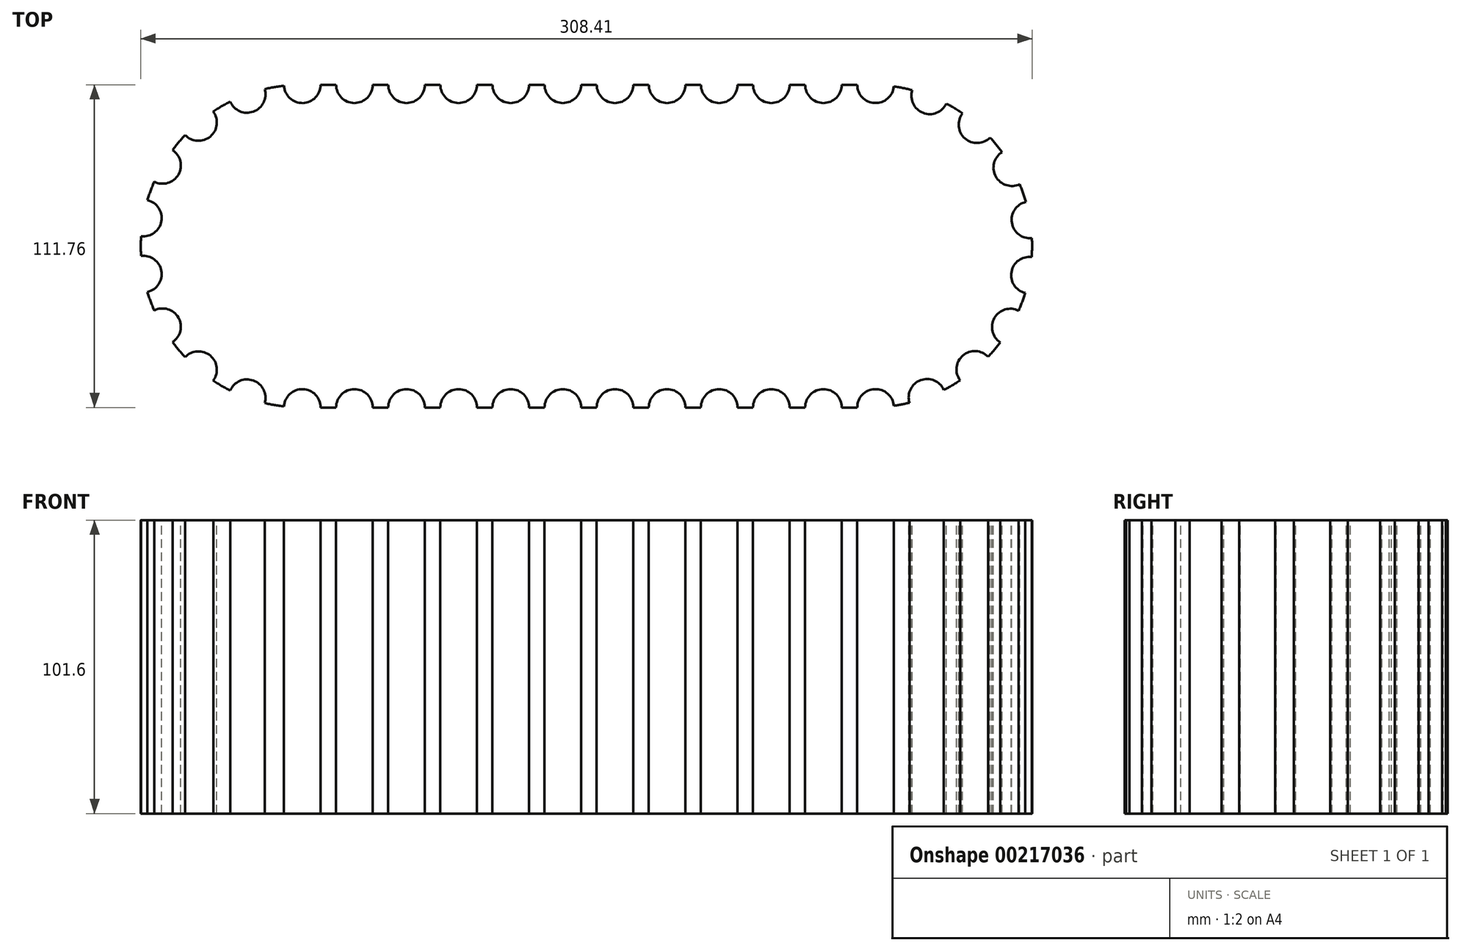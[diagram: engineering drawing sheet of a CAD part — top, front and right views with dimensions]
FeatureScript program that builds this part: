
annotation { "Feature Type Name" : "Feature", "Feature Type Description" : "" }
export const myFeature = defineFeature(function(context is Context, id is Id, definition is map)
    precondition{}
    {
        {
            var Q0;
            Q0=qCreatedBy(makeId("Top.planeOp"),FACE);
            var sketch = newSketch(context, id + "F0", { "sketchPlane" : qUnion([Q0])});
            skArc(sketch, "E0", {"start": v(-196.65, 55.88) * mm, "mid": v(-252.53, 0) * mm, "end": v(-196.65, -55.88) * mm});
            skArc(sketch, "E1", {"start": v(0, -55.88) * mm, "mid": v(55.88, 0) * mm, "end": v(0, 55.88) * mm});
            skLineSegment(sketch, "E2", {"start": v(-196.65, 55.88) * mm, "end": v(0, 55.88) * mm});
            skLineSegment(sketch, "E3", {"start": v(-196.65, -55.88) * mm, "end": v(0, -55.88) * mm});
            skSolve(sketch);
        }
        {
            var Q0;
            Q0=makeQuery(id+"F0.imprint","IMPRINT",FACE,{"disambiguationData":[TD([[makeQuery(id+"F0.imprint","IMPRINT",EDGE,{"derivedFrom":sQuery(id+"F0.wireOp",EDGE,"E0")}),1.0]])]});
            extrude(context, id + "F1", {"entities" : qUnion([Q0]), "depth" : 101.6 * mm});
        }
        {
            var Q0;
            Q0=makeQuery(id+"F1.opExtrude","CAP_FACE",FACE,{"disambiguationData":[OSD([sQuery(id+"F0.wireOp",EDGE,"E0"),sQuery(id+"F0.wireOp",EDGE,"E1"),sQuery(id+"F0.wireOp",EDGE,"E2"),sQuery(id+"F0.wireOp",EDGE,"E3")])],"isStart":false});
            var sketch = newSketch(context, id + "F2", { "sketchPlane" : qUnion([Q0])});
            skCircle(sketch, "E4", {"center": v(-196.65, 55.88) * mm, "radius": 6.35 * mm});
            skCircle(sketch, "E5.1.0.0", {"center": v(-178.61, 55.88) * mm, "radius": 6.35 * mm});
            skCircle(sketch, "E5.2.0.0", {"center": v(-160.58, 55.88) * mm, "radius": 6.35 * mm});
            skCircle(sketch, "E5.3.0.0", {"center": v(-142.54, 55.88) * mm, "radius": 6.35 * mm});
            skCircle(sketch, "E5.4.0.0", {"center": v(-124.51, 55.88) * mm, "radius": 6.35 * mm});
            skCircle(sketch, "E5.5.0.0", {"center": v(-106.48, 55.88) * mm, "radius": 6.35 * mm});
            skCircle(sketch, "E5.6.0.0", {"center": v(-88.44, 55.88) * mm, "radius": 6.35 * mm});
            skCircle(sketch, "E5.7.0.0", {"center": v(-70.4, 55.88) * mm, "radius": 6.35 * mm});
            skCircle(sketch, "E5.8.0.0", {"center": v(-52.37, 55.88) * mm, "radius": 6.35 * mm});
            skCircle(sketch, "E5.9.0.0", {"center": v(-34.34, 55.88) * mm, "radius": 6.35 * mm});
            skCircle(sketch, "E5.10.0.0", {"center": v(-16.3, 55.88) * mm, "radius": 6.35 * mm});
            skCircle(sketch, "E5.11.0.0", {"center": v(1.73, 55.88) * mm, "radius": 6.35 * mm});
            skLineSegment(sketch, "E5.direction1", {"start": v(-196.65, 55.88) * mm, "end": v(-178.61, 55.88) * mm, "construction": true});
            skCircle(sketch, "E6", {"center": v(-196.65, -55.88) * mm, "radius": 6.35 * mm});
            skCircle(sketch, "E7.1.0.0", {"center": v(-178.61, -55.88) * mm, "radius": 6.35 * mm});
            skCircle(sketch, "E7.2.0.0", {"center": v(-160.58, -55.88) * mm, "radius": 6.35 * mm});
            skCircle(sketch, "E7.3.0.0", {"center": v(-142.54, -55.88) * mm, "radius": 6.35 * mm});
            skCircle(sketch, "E7.4.0.0", {"center": v(-124.51, -55.88) * mm, "radius": 6.35 * mm});
            skCircle(sketch, "E7.5.0.0", {"center": v(-106.48, -55.88) * mm, "radius": 6.35 * mm});
            skCircle(sketch, "E7.6.0.0", {"center": v(-88.44, -55.88) * mm, "radius": 6.35 * mm});
            skCircle(sketch, "E7.7.0.0", {"center": v(-70.4, -55.88) * mm, "radius": 6.35 * mm});
            skCircle(sketch, "E7.8.0.0", {"center": v(-52.37, -55.88) * mm, "radius": 6.35 * mm});
            skCircle(sketch, "E7.9.0.0", {"center": v(-34.34, -55.88) * mm, "radius": 6.35 * mm});
            skCircle(sketch, "E7.10.0.0", {"center": v(-16.3, -55.88) * mm, "radius": 6.35 * mm});
            skCircle(sketch, "E7.11.0.0", {"center": v(1.73, -55.88) * mm, "radius": 6.35 * mm});
            skLineSegment(sketch, "E7.direction1", {"start": v(-196.65, -55.88) * mm, "end": v(-178.61, -55.88) * mm, "construction": true});
            skCircle(sketch, "E8.1.0", {"center": v(-215.76, 52.51) * mm, "radius": 6.35 * mm});
            skCircle(sketch, "E8.2.0", {"center": v(-232.57, 42.8) * mm, "radius": 6.35 * mm});
            skCircle(sketch, "E8.3.0", {"center": v(-245.04, 27.94) * mm, "radius": 6.35 * mm});
            skCircle(sketch, "E8.4.0", {"center": v(-251.68, 9.7) * mm, "radius": 6.35 * mm});
            skCircle(sketch, "E8.5.0", {"center": v(-251.68, -9.7) * mm, "radius": 6.35 * mm});
            skCircle(sketch, "E8.6.0", {"center": v(-245.04, -27.94) * mm, "radius": 6.35 * mm});
            skCircle(sketch, "E8.7.0", {"center": v(-232.57, -42.8) * mm, "radius": 6.35 * mm});
            skCircle(sketch, "E8.8.0", {"center": v(-215.76, -52.51) * mm, "radius": 6.35 * mm});
            skPoint(sketch, "E8.center", {"position": v(-196.65, 0) * mm});
            skLineSegment(sketch, "E8.anchor1", {"start": v(-196.65, 0) * mm, "end": v(-196.65, 55.88) * mm, "construction": true});
            skLineSegment(sketch, "E8.anchor2", {"start": v(-196.65, 0) * mm, "end": v(-196.65, -55.88) * mm, "construction": true});
            skCircle(sketch, "E9.1.0", {"center": v(20.48, 52.02) * mm, "radius": 6.35 * mm});
            skCircle(sketch, "E9.2.0", {"center": v(36.84, 42.06) * mm, "radius": 6.35 * mm});
            skCircle(sketch, "E9.3.0", {"center": v(48.87, 27.16) * mm, "radius": 6.35 * mm});
            skCircle(sketch, "E9.4.0", {"center": v(55.17, 9.07) * mm, "radius": 6.35 * mm});
            skCircle(sketch, "E9.5.0", {"center": v(55, -10.07) * mm, "radius": 6.35 * mm});
            skCircle(sketch, "E9.6.0", {"center": v(48.37, -28.04) * mm, "radius": 6.35 * mm});
            skCircle(sketch, "E9.7.0", {"center": v(36.07, -42.72) * mm, "radius": 6.35 * mm});
            skCircle(sketch, "E9.8.0", {"center": v(19.53, -52.38) * mm, "radius": 6.35 * mm});
            skArc(sketch, "E9.9.0", {"start": v(1.08, -49.56) * mm, "mid": v(0.86, -49.55) * mm, "end": v(0.63, -49.55) * mm});
            skPoint(sketch, "E9.center", {"position": v(0, 0) * mm});
            skLineSegment(sketch, "E9.anchor2", {"start": v(0.63, -49.55) * mm, "end": v(0.63, -49.63) * mm, "construction": true});
            skSolve(sketch);
        }
        {
            var Q0;
            Q0 = qSketchRegion(id + "F2", true);
            extrude(context, id + "F3", {"entities" : qUnion([Q0]), "operationType" : NewBodyOperationType.REMOVE, "endBound" : BoundingType.THROUGH_ALL, "oppositeDirection" : true, "depth" : 25.4 * mm});
        }
    });
